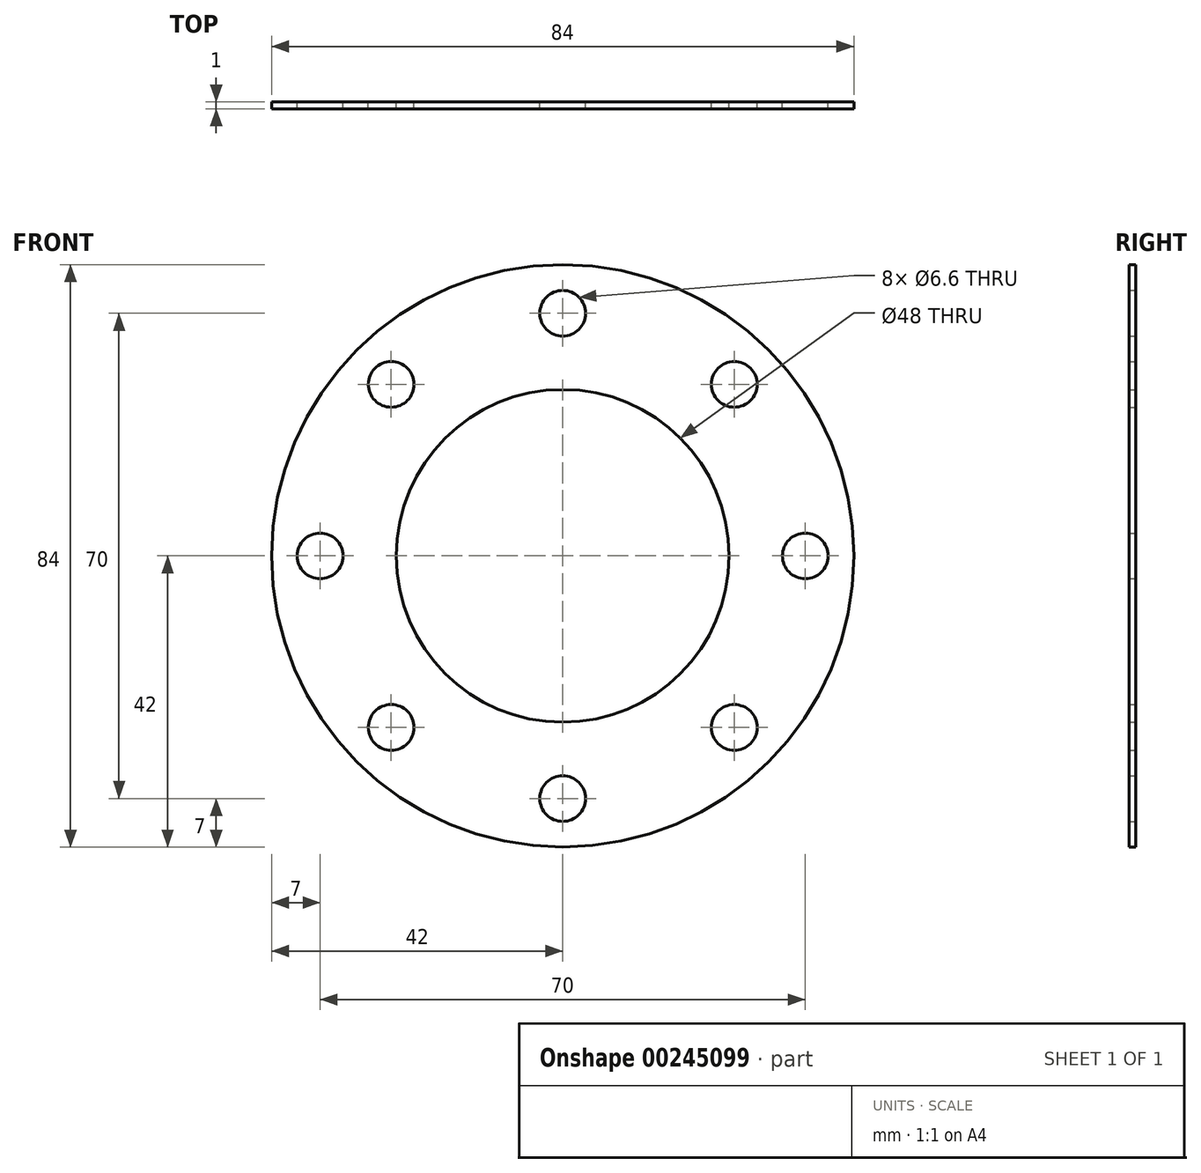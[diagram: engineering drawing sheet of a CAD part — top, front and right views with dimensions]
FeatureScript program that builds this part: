
annotation { "Feature Type Name" : "Feature", "Feature Type Description" : "" }
export const myFeature = defineFeature(function(context is Context, id is Id, definition is map)
    precondition{}
    {
        {
            var Q0;
            Q0=qCreatedBy(makeId("Front.planeOp"),FACE);
            var sketch = newSketch(context, id + "F0", { "sketchPlane" : qUnion([Q0])});
            skCircle(sketch, "E0", {"center": v(0, 0) * mm, "radius": 35 * mm});
            skCircle(sketch, "E1", {"center": v(0, 0) * mm, "radius": 24 * mm});
            skCircle(sketch, "E2", {"center": v(0, 0) * mm, "radius": 42 * mm});
            skCircle(sketch, "E3", {"center": v(0, 35) * mm, "radius": 3.3 * mm});
            skCircle(sketch, "E4.1.0", {"center": v(-24.75, 24.75) * mm, "radius": 3.3 * mm});
            skCircle(sketch, "E4.2.0", {"center": v(-35, 0) * mm, "radius": 3.3 * mm});
            skCircle(sketch, "E5.1.3.0", {"center": v(-24.75, -24.75) * mm, "radius": 3.3 * mm});
            skCircle(sketch, "E5.1.4.0", {"center": v(0, -35) * mm, "radius": 3.3 * mm});
            skCircle(sketch, "E5.1.5.0", {"center": v(24.75, -24.75) * mm, "radius": 3.3 * mm});
            skCircle(sketch, "E5.1.6.0", {"center": v(35, 0) * mm, "radius": 3.3 * mm});
            skCircle(sketch, "E5.1.7.0", {"center": v(24.75, 24.75) * mm, "radius": 3.3 * mm});
            skSolve(sketch);
        }
        {
            var Q0;
            Q0 = qSketchRegion(id + "F0", true);
            var Q1;
            Q1=makeQuery(id+"F0.imprint","IMPRINT",FACE,{"disambiguationData":[TD([[makeQuery(id+"F0.imprint","IMPRINT",EDGE,{"derivedFrom":sQuery(id+"F0.wireOp",EDGE,"E1")}),-1.0]])]});
            extrude(context, id + "F1", {"entities" : qUnion([Q0, Q1]), "endBound" : BoundingType.SYMMETRIC, "depth" : 1 * mm});
        }
    });
